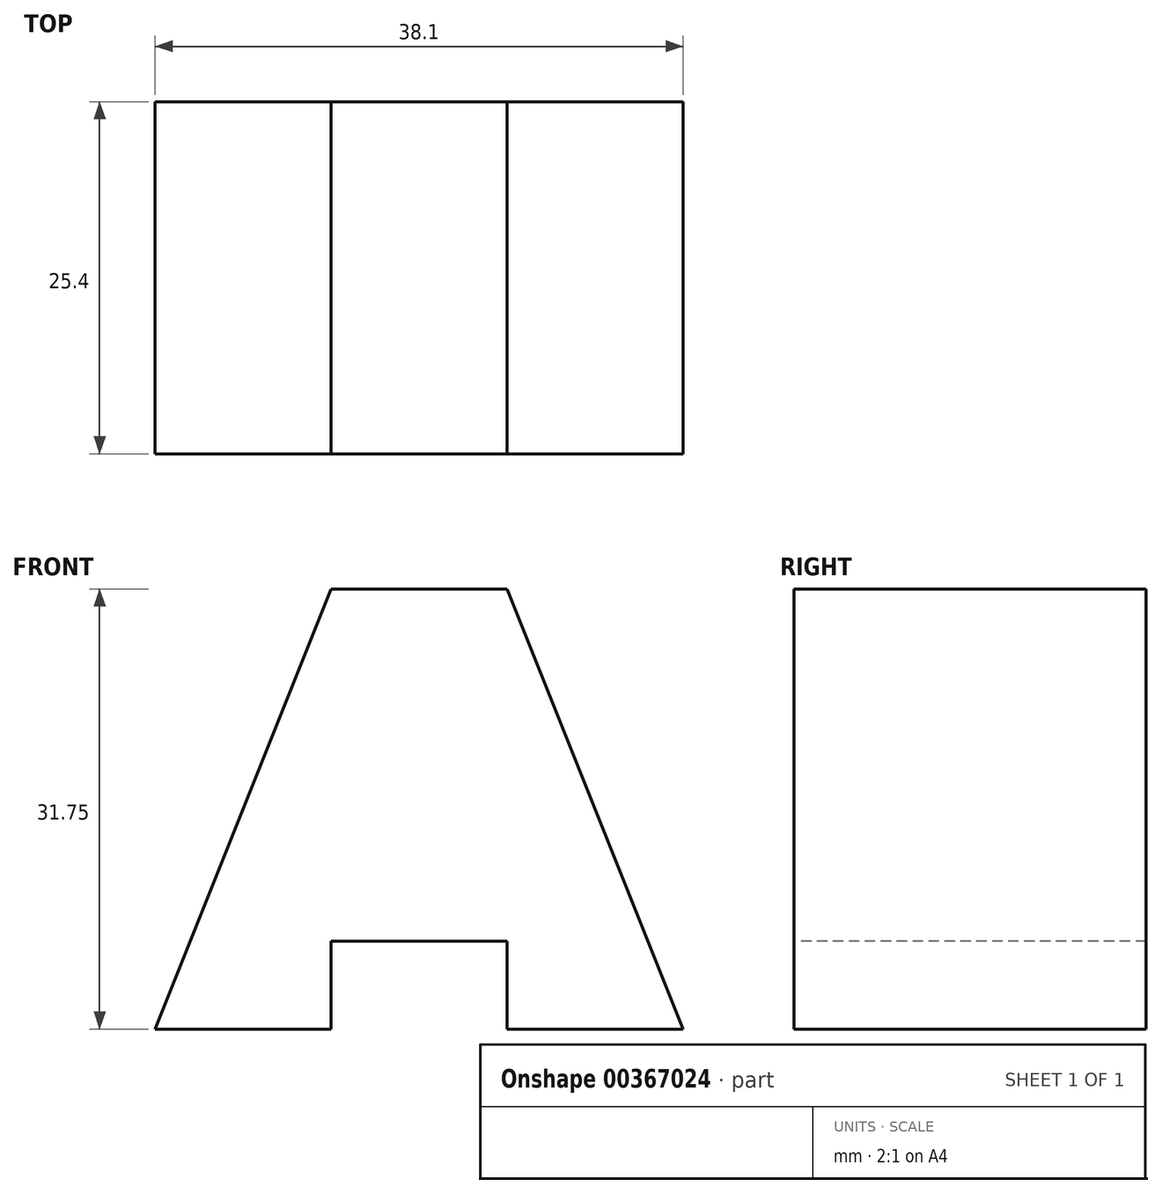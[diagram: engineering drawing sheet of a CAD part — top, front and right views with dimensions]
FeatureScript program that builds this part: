
annotation { "Feature Type Name" : "Feature", "Feature Type Description" : "" }
export const myFeature = defineFeature(function(context is Context, id is Id, definition is map)
    precondition{}
    {
        {
            var Q0;
            Q0=qCreatedBy(makeId("Front.planeOp"),FACE);
            var sketch = newSketch(context, id + "F0", { "sketchPlane" : qUnion([Q0])});
            skLineSegment(sketch, "E0", {"start": v(0, 0) * mm, "end": v(38.1, 0) * mm});
            skLineSegment(sketch, "E1", {"start": v(38.1, 0) * mm, "end": v(38.1, 31.75) * mm});
            skLineSegment(sketch, "E2", {"start": v(38.1, 31.75) * mm, "end": v(0, 31.75) * mm});
            skLineSegment(sketch, "E3", {"start": v(0, 31.75) * mm, "end": v(0, 0) * mm});
            skSolve(sketch);
        }
        {
            var Q0;
            Q0 = qSketchRegion(id + "F0", true);
            extrude(context, id + "F1", {"entities" : qUnion([Q0]), "depth" : 25.4 * mm});
        }
        {
            var Q0;
            Q0=makeQuery(id+"F1.opExtrude","CAP_FACE",FACE,{"disambiguationData":[OSD([sQuery(id+"F0.wireOp",EDGE,"E0"),sQuery(id+"F0.wireOp",EDGE,"E1"),sQuery(id+"F0.wireOp",EDGE,"E2"),sQuery(id+"F0.wireOp",EDGE,"E3")])],"isStart":false});
            var sketch = newSketch(context, id + "F2", { "sketchPlane" : qUnion([Q0])});
            skLineSegment(sketch, "E4", {"start": v(12.7, 0) * mm, "end": v(12.7, 6.35) * mm});
            skLineSegment(sketch, "E5", {"start": v(12.7, 6.35) * mm, "end": v(25.4, 6.35) * mm});
            skLineSegment(sketch, "E6", {"start": v(25.4, 6.35) * mm, "end": v(25.4, 0) * mm});
            skSolve(sketch);
        }
        {
            var Q0;
            Q0 = qSketchRegion(id + "F2", true);
            var Q1;
            {var subQ0=sQuery(id+"F2.wireOp",EDGE,"E4");Q1=makeQuery(id+"F2.imprint","IMPRINT",FACE,{"disambiguationData":[TD([[makeQuery(id+"F2.imprint","IMPRINT",EDGE,{"derivedFrom":subQ0}),-1.0]])]});}
            extrude(context, id + "F3", {"entities" : qUnion([Q0, Q1]), "operationType" : NewBodyOperationType.REMOVE, "oppositeDirection" : true, "depth" : 25.4 * mm});
        }
        {
            var Q0;
            Q0=makeQuery(id+"F1.opExtrude","CAP_FACE",FACE,{"disambiguationData":[OSD([sQuery(id+"F0.wireOp",EDGE,"E0"),sQuery(id+"F0.wireOp",EDGE,"E1"),sQuery(id+"F0.wireOp",EDGE,"E2"),sQuery(id+"F0.wireOp",EDGE,"E3")])],"isStart":false});
            var sketch = newSketch(context, id + "F4", { "sketchPlane" : qUnion([Q0])});
            skLineSegment(sketch, "E7", {"start": v(25.4, 31.75) * mm, "end": v(38.1, 0) * mm});
            skLineSegment(sketch, "E8", {"start": v(12.7, 31.75) * mm, "end": v(0, 0) * mm});
            skSolve(sketch);
        }
        {
            var Q0;
            Q0 = qSketchRegion(id + "F4", true);
            var Q1;
            {var subQ0=sQuery(id+"F4.wireOp",EDGE,"E8");Q1=makeQuery(id+"F4.imprint","IMPRINT",FACE,{"disambiguationData":[TD([[makeQuery(id+"F4.imprint","IMPRINT",EDGE,{"derivedFrom":subQ0}),-1.0]])]});}
            var Q2;
            {var subQ0=sQuery(id+"F4.wireOp",EDGE,"E7");Q2=makeQuery(id+"F4.imprint","IMPRINT",FACE,{"disambiguationData":[TD([[makeQuery(id+"F4.imprint","IMPRINT",EDGE,{"derivedFrom":subQ0}),1.0]])]});}
            extrude(context, id + "F5", {"entities" : qUnion([Q0, Q1, Q2]), "operationType" : NewBodyOperationType.REMOVE, "oppositeDirection" : true, "depth" : 25.4 * mm});
        }
    });
